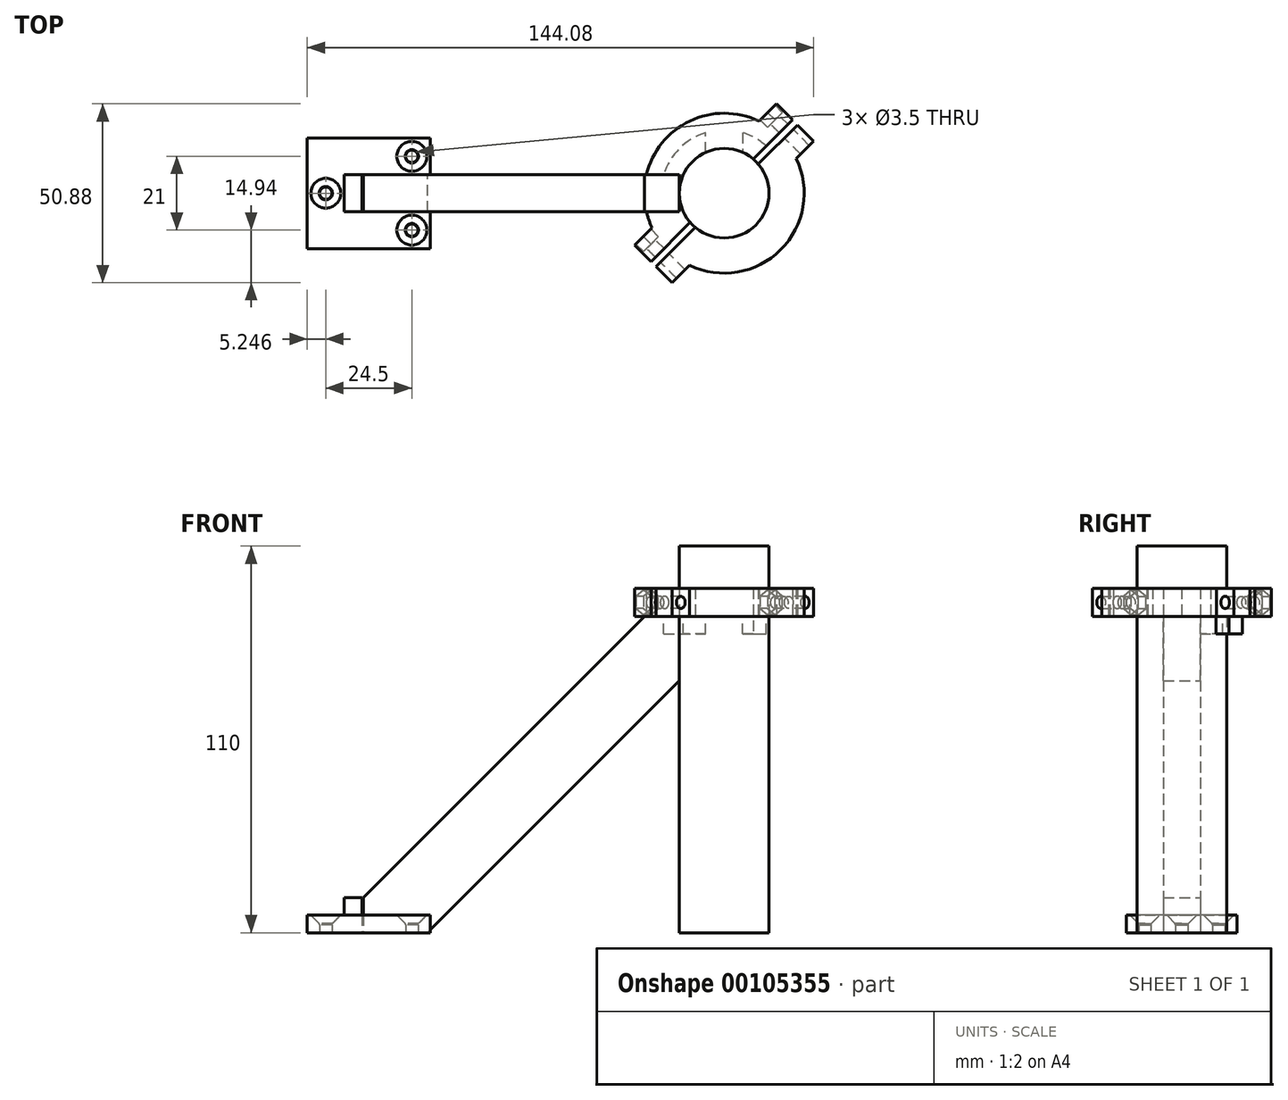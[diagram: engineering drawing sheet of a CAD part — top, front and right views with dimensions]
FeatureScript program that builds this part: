
annotation { "Feature Type Name" : "Feature", "Feature Type Description" : "" }
export const myFeature = defineFeature(function(context is Context, id is Id, definition is map)
    precondition{}
    {
        {
            var Q0;
            Q0=qCreatedBy(makeId("Top.planeOp"),FACE);
            var sketch = newSketch(context, id + "F0", { "sketchPlane" : qUnion([Q0])});
            skCircle(sketch, "E0", {"center": v(0, 0) * mm, "radius": 12.75 * mm});
            skLineSegment(sketch, "E1.bottom", {"start": v(-83.64, 15.75) * mm, "end": v(-118.64, 15.75) * mm});
            skLineSegment(sketch, "E1.top", {"start": v(-83.64, -15.75) * mm, "end": v(-118.64, -15.75) * mm});
            skLineSegment(sketch, "E1.left", {"start": v(-83.64, 15.75) * mm, "end": v(-83.64, 5.25) * mm});
            skLineSegment(sketch, "E1.right", {"start": v(-118.64, 15.75) * mm, "end": v(-118.64, -15.75) * mm});
            skLineSegment(sketch, "E2.bottom", {"start": v(-83.64, -5.25) * mm, "end": v(-108.14, -5.25) * mm});
            skLineSegment(sketch, "E2.top", {"start": v(-83.64, 5.25) * mm, "end": v(-108.14, 5.25) * mm});
            skLineSegment(sketch, "E2.right", {"start": v(-108.14, -5.25) * mm, "end": v(-108.14, 5.25) * mm});
            skCircle(sketch, "E3", {"center": v(-88.9, 10.5) * mm, "radius": 1.75 * mm});
            skCircle(sketch, "E4", {"center": v(-113.4, 0) * mm, "radius": 1.75 * mm});
            skCircle(sketch, "E5.MirrorC", {"center": v(-88.9, -10.5) * mm, "radius": 1.75 * mm});
            skCircle(sketch, "E6", {"center": v(-88.9, 10.5) * mm, "radius": 4.25 * mm, "construction": true});
            skCircle(sketch, "E7", {"center": v(-113.4, 0) * mm, "radius": 4.25 * mm, "construction": true});
            skLineSegment(sketch, "E8", {"start": v(-103.14, 5.25) * mm, "end": v(-103.14, -5.25) * mm});
            skLineSegment(sketch, "E9.trimOffspring", {"start": v(-83.64, -5.25) * mm, "end": v(-83.64, -15.75) * mm});
            skSolve(sketch);
        }
        {
            var Q0;
            Q0=makeQuery(id+"F0.imprint","IMPRINT",FACE,{"disambiguationData":[TD([[makeQuery(id+"F0.imprint","IMPRINT",EDGE,{"derivedFrom":sQuery(id+"F0.wireOp",EDGE,"E1.bottom")}),1.0]])]});
            extrude(context, id + "F1", {"entities" : qUnion([Q0]), "depth" : 5 * mm});
        }
        {
            var Q0;
            {var subQ0=sQuery(id+"F0.wireOp",EDGE,"E2.right");Q0=makeQuery(id+"F0.imprint","IMPRINT",FACE,{"disambiguationData":[TD([[makeQuery(id+"F0.imprint","IMPRINT",EDGE,{"derivedFrom":subQ0}),-1.0]])]});}
            extrude(context, id + "F2", {"entities" : qUnion([Q0]), "operationType" : NewBodyOperationType.ADD, "depth" : 10 * mm});
        }
        {
            var Q0;
            Q0=makeQuery(id+"F1.opExtrude","CAP_EDGE",EDGE,{"disambiguationData":[OSD([sQuery(id+"F0.wireOp",EDGE,"E4")])],"isStart":false});
            var Q1;
            Q1=makeQuery(id+"F1.opExtrude","CAP_EDGE",EDGE,{"disambiguationData":[OSD([sQuery(id+"F0.wireOp",EDGE,"E3")])],"isStart":false});
            var Q2;
            Q2=makeQuery(id+"F1.opExtrude","CAP_EDGE",EDGE,{"disambiguationData":[OSD([sQuery(id+"F0.wireOp",EDGE,"E5.MirrorC")])],"isStart":false});
            chamfer(context, id + "F3", {"entities" : qUnion([Q0, Q1, Q2]), "width" : 2.5 * mm, "tangentPropagation" : true});
        }
        {
            var Q0;
            {var subQ0=sQuery(id+"F0.wireOp",EDGE,"E4");Q0=makeQuery(id+"F3.opChamfer","BLEND_EDGE",EDGE,{"blendedFrom":[makeQuery(id+"F1.opExtrude","CAP_EDGE",EDGE,{"disambiguationData":[OSD([subQ0])],"isStart":false}),makeQuery(id+"F1.opExtrude","SWEPT_FACE",FACE,{"disambiguationData":[OSD([subQ0])]})],"blendedInto":[makeQuery(id+"F1.opExtrude","SWEPT_FACE",FACE,{"disambiguationData":[OSD([subQ0])]})]});}
            var Q1;
            {var subQ0=sQuery(id+"F0.wireOp",EDGE,"E3");Q1=makeQuery(id+"F3.opChamfer","BLEND_EDGE",EDGE,{"blendedFrom":[makeQuery(id+"F1.opExtrude","CAP_EDGE",EDGE,{"disambiguationData":[OSD([subQ0])],"isStart":false}),makeQuery(id+"F1.opExtrude","SWEPT_FACE",FACE,{"disambiguationData":[OSD([subQ0])]})],"blendedInto":[makeQuery(id+"F1.opExtrude","SWEPT_FACE",FACE,{"disambiguationData":[OSD([subQ0])]})]});}
            var Q2;
            {var subQ0=sQuery(id+"F0.wireOp",EDGE,"E5.MirrorC");Q2=makeQuery(id+"F3.opChamfer","BLEND_EDGE",EDGE,{"blendedFrom":[makeQuery(id+"F1.opExtrude","CAP_EDGE",EDGE,{"disambiguationData":[OSD([subQ0])],"isStart":false}),makeQuery(id+"F1.opExtrude","SWEPT_FACE",FACE,{"disambiguationData":[OSD([subQ0])]})],"blendedInto":[makeQuery(id+"F1.opExtrude","SWEPT_FACE",FACE,{"disambiguationData":[OSD([subQ0])]})]});}
            chamfer(context, id + "F4", {"entities" : qUnion([Q0, Q1, Q2]), "width" : 0.5 * mm, "tangentPropagation" : true});
        }
        {
            var Q0;
            Q0=makeQuery(id+"F0.imprint","IMPRINT",FACE,{"disambiguationData":[TD([[makeQuery(id+"F0.imprint","IMPRINT",EDGE,{"derivedFrom":sQuery(id+"F0.wireOp",EDGE,"E0")}),1.0]])]});
            extrude(context, id + "F5", {"entities" : qUnion([Q0]), "depth" : 110 * mm});
        }
        {
            var Q0;
            Q0=qCreatedBy(makeId("Front.planeOp"),FACE);
            var sketch = newSketch(context, id + "F6", { "sketchPlane" : qUnion([Q0])});
            skLineSegment(sketch, "E10", {"start": v(-12.75, 0) * mm, "end": v(-12.75, 90) * mm});
            skLineSegment(sketch, "E11", {"start": v(-12.75, 71.72) * mm, "end": v(-84.47, 0) * mm});
            skLineSegment(sketch, "E12", {"start": v(-22.75, 90) * mm, "end": v(-102.75, 10) * mm});
            skLineSegment(sketch, "E13", {"start": v(-102.75, 10) * mm, "end": v(-102.75, 0) * mm});
            skLineSegment(sketch, "E14", {"start": v(-102.75, 0) * mm, "end": v(-84.47, 0) * mm});
            skLineSegment(sketch, "E15", {"start": v(-22.75, 90) * mm, "end": v(-12.75, 90) * mm});
            skSolve(sketch);
        }
        {
            var Q0;
            Q0 = qSketchRegion(id + "F6", true);
            extrude(context, id + "F7", {"entities" : qUnion([Q0]), "endBound" : BoundingType.SYMMETRIC, "depth" : 10.5 * mm});
        }
        {
            var Q0;
            Q0=makeQuery(id+"F7.opExtrude","SWEPT_FACE",FACE,{"disambiguationData":[OSD([sQuery(id+"F6.wireOp",EDGE,"E15")])]});
            var sketch = newSketch(context, id + "F8", { "sketchPlane" : qUnion([Q0])});
            skCircle(sketch, "E16.0", {"center": v(0, 0) * mm, "radius": 12.75 * mm});
            skLineSegment(sketch, "E17.0", {"start": v(-22.75, -5.25) * mm, "end": v(-22.75, 5.25) * mm, "construction": true});
            skPoint(sketch, "E18", {"position": v(-22.75, 0) * mm});
            skLineSegment(sketch, "E19", {"start": v(-33.02, -33.02) * mm, "end": v(44.09, 44.09) * mm, "construction": true});
            skLineSegment(sketch, "E20", {"start": v(8.28, 9.7) * mm, "end": v(19.43, 20.84) * mm});
            skLineSegment(sketch, "E21", {"start": v(19.43, 20.84) * mm, "end": v(14.83, 25.44) * mm});
            skLineSegment(sketch, "E22", {"start": v(14.83, 25.44) * mm, "end": v(9.88, 20.5) * mm});
            skLineSegment(sketch, "E23", {"start": v(30.41, -30.41) * mm, "end": v(-33.98, 33.98) * mm, "construction": true});
            skLineSegment(sketch, "E24.MirrorCS", {"start": v(-25.44, -14.83) * mm, "end": v(-20.5, -9.88) * mm});
            skLineSegment(sketch, "E25.MirrorCS", {"start": v(-20.84, -19.43) * mm, "end": v(-25.44, -14.83) * mm});
            skLineSegment(sketch, "E26.MirrorCS", {"start": v(-9.7, -8.28) * mm, "end": v(-20.84, -19.43) * mm});
            skArc(sketch, "E27", {"start": v(-20.5, -9.88) * mm, "mid": v(-22.43, 3.8) * mm, "end": v(-16.09, 16.09) * mm});
            skArc(sketch, "E28.MirrorCS", {"start": v(9.88, 20.5) * mm, "mid": v(-3.8, 22.43) * mm, "end": v(-16.09, 16.09) * mm});
            skLineSegment(sketch, "E29.MirrorCS", {"start": v(9.7, 8.28) * mm, "end": v(20.84, 19.43) * mm});
            skLineSegment(sketch, "E30.MirrorCS", {"start": v(20.84, 19.43) * mm, "end": v(25.44, 14.83) * mm});
            skLineSegment(sketch, "E31.MirrorCS", {"start": v(25.44, 14.83) * mm, "end": v(20.5, 9.88) * mm});
            skArc(sketch, "E32.MirrorCS", {"start": v(20.5, 9.88) * mm, "mid": v(22.43, -3.8) * mm, "end": v(16.09, -16.09) * mm});
            skArc(sketch, "E33.MirrorCS", {"start": v(-9.88, -20.5) * mm, "mid": v(3.8, -22.43) * mm, "end": v(16.09, -16.09) * mm});
            skLineSegment(sketch, "E34.MirrorCS", {"start": v(-14.83, -25.44) * mm, "end": v(-9.88, -20.5) * mm});
            skLineSegment(sketch, "E35.MirrorCS", {"start": v(-19.43, -20.84) * mm, "end": v(-14.83, -25.44) * mm});
            skLineSegment(sketch, "E36.MirrorCS", {"start": v(-8.28, -9.7) * mm, "end": v(-19.43, -20.84) * mm});
            skSolve(sketch);
        }
        {
            var Q0;
            {var subQ0=sQuery(id+"F8.wireOp",EDGE,"E20");Q0=makeQuery(id+"F8.imprint","IMPRINT",FACE,{"disambiguationData":[TD([[makeQuery(id+"F8.imprint","IMPRINT",EDGE,{"derivedFrom":subQ0}),1.0]])]});}
            var Q1;
            {var subQ0=sQuery(id+"F8.wireOp",EDGE,"E29.MirrorCS");Q1=makeQuery(id+"F8.imprint","IMPRINT",FACE,{"disambiguationData":[TD([[makeQuery(id+"F8.imprint","IMPRINT",EDGE,{"derivedFrom":subQ0}),-1.0]])]});}
            var Q2;
            {var subQ0=sQuery(id+"F6.wireOp",EDGE,"E15");var subQ1=makeQuery(id+"F7.opExtrude","CAP_EDGE",EDGE,{"disambiguationData":[OSD([subQ0])],"isStart":false});var subQ5=sQuery(id+"F8.wireOp",EDGE,"E27");var subQ10=makeQuery(id+"F8.imprint","INTERSECT",VERTEX,{"derivedFrom":[subQ1,subQ5]});Q2=makeQuery(id+"F8.imprint","IMPRINT",FACE,{"disambiguationData":[TD([[makeQuery(id+"F8.imprint","IMPRINT",EDGE,{"disambiguationData":[TD([[subQ10,-1.0]])],"derivedFrom":subQ5}),-1.0]])]});}
            var Q3;
            {var subQ7=sQuery(id+"F8.wireOp",EDGE,"E24.MirrorCS");Q3=makeQuery(id+"F8.imprint","IMPRINT",FACE,{"disambiguationData":[TD([[makeQuery(id+"F8.imprint","IMPRINT",EDGE,{"derivedFrom":subQ7}),-1.0]])]});}
            extrude(context, id + "F9", {"entities" : qUnion([Q0, Q1, Q2, Q3]), "depth" : 8 * mm});
        }
        {
            var Q0;
            Q0=makeQuery(id+"F9.opExtrude","CAP_FACE",FACE,{"disambiguationData":[OSD([sQuery(id+"F8.wireOp",EDGE,"E16.0"),sQuery(id+"F8.wireOp",EDGE,"E20"),sQuery(id+"F8.wireOp",EDGE,"E21"),sQuery(id+"F8.wireOp",EDGE,"E22"),sQuery(id+"F8.wireOp",EDGE,"E24.MirrorCS"),sQuery(id+"F8.wireOp",EDGE,"E25.MirrorCS"),sQuery(id+"F8.wireOp",EDGE,"E26.MirrorCS"),sQuery(id+"F8.wireOp",EDGE,"E27"),sQuery(id+"F8.wireOp",EDGE,"E28.MirrorCS")])],"isStart":true});
            var sketch = newSketch(context, id + "F10", { "sketchPlane" : qUnion([Q0])});
            skLineSegment(sketch, "E37.0", {"start": v(30.41, 30.41) * mm, "end": v(-33.98, -33.98) * mm, "construction": true});
            skLineSegment(sketch, "E38.0", {"start": v(-12.75, -5.25) * mm, "end": v(-84.47, -5.25) * mm});
            skLineSegment(sketch, "E39.0", {"start": v(-12.75, 5.25) * mm, "end": v(-84.47, 5.25) * mm});
            skLineSegment(sketch, "E40.0", {"start": v(-9.7, 8.28) * mm, "end": v(-20.84, 19.43) * mm});
            skLineSegment(sketch, "E41", {"start": v(-12.75, 5.25) * mm, "end": v(-11.62, 5.25) * mm});
            skLineSegment(sketch, "E42", {"start": v(-12.75, -5.25) * mm, "end": v(-11.62, -5.25) * mm});
            skArc(sketch, "E43", {"start": v(-13.42, 12) * mm, "mid": v(-15.68, 8.83) * mm, "end": v(-17.22, 5.25) * mm});
            skArc(sketch, "E44", {"start": v(-17.22, -5.25) * mm, "mid": v(-15.43, -9.26) * mm, "end": v(-12.73, -12.73) * mm});
            skArc(sketch, "E45.MirrorCS", {"start": v(-5.25, -17.22) * mm, "mid": v(-9.26, -15.43) * mm, "end": v(-12.73, -12.73) * mm});
            skLineSegment(sketch, "E46.MirrorCS", {"start": v(-5.25, -12.75) * mm, "end": v(-5.25, -84.47) * mm});
            skLineSegment(sketch, "E47.MirrorCS", {"start": v(-5.25, -12.75) * mm, "end": v(-5.25, -11.62) * mm});
            skLineSegment(sketch, "E48.MirrorCS", {"start": v(5.25, -12.75) * mm, "end": v(5.25, -11.62) * mm});
            skLineSegment(sketch, "E49.MirrorCS", {"start": v(5.25, -12.75) * mm, "end": v(5.25, -84.47) * mm});
            skArc(sketch, "E50.MirrorCS", {"start": v(12, -13.42) * mm, "mid": v(8.83, -15.68) * mm, "end": v(5.25, -17.22) * mm});
            skLineSegment(sketch, "E51.MirrorCS", {"start": v(8.28, -9.7) * mm, "end": v(19.43, -20.84) * mm});
            skSolve(sketch);
        }
        {
            var Q0;
            {var subQ6=sQuery(id+"F10.wireOp",EDGE,"E41");Q0=makeQuery(id+"F10.imprint","IMPRINT",FACE,{"disambiguationData":[TD([[makeQuery(id+"F10.imprint","IMPRINT",EDGE,{"derivedFrom":subQ6}),1.0]])]});}
            var Q1;
            {var subQ1=sQuery(id+"F10.wireOp",EDGE,"E42");Q1=makeQuery(id+"F10.imprint","IMPRINT",FACE,{"disambiguationData":[TD([[makeQuery(id+"F10.imprint","IMPRINT",EDGE,{"derivedFrom":subQ1}),-1.0]])]});}
            var Q2;
            {var subQ6=sQuery(id+"F10.wireOp",EDGE,"E48.MirrorCS");Q2=makeQuery(id+"F10.imprint","IMPRINT",FACE,{"disambiguationData":[TD([[makeQuery(id+"F10.imprint","IMPRINT",EDGE,{"derivedFrom":subQ6}),-1.0]])]});}
            extrude(context, id + "F11", {"entities" : qUnion([Q0, Q1, Q2]), "operationType" : NewBodyOperationType.ADD, "depth" : 5 * mm});
        }
        {
            var Q0;
            Q0=makeQuery(id+"F9.opExtrude","SWEPT_FACE",FACE,{"disambiguationData":[OSD([sQuery(id+"F8.wireOp",EDGE,"E22")])]});
            var sketch = newSketch(context, id + "F12", { "sketchPlane" : qUnion([Q0])});
            skPoint(sketch, "E52.0", {"position": v(-28.48, 98) * mm});
            skPoint(sketch, "E53.0", {"position": v(-21.48, 90) * mm});
            skPoint(sketch, "E54.0", {"position": v(21.48, 98) * mm});
            skPoint(sketch, "E55.0", {"position": v(28.48, 90) * mm});
            skLineSegment(sketch, "E56", {"start": v(-28.48, 98) * mm, "end": v(-21.48, 90) * mm, "construction": true});
            skLineSegment(sketch, "E57", {"start": v(21.48, 98) * mm, "end": v(28.48, 90) * mm, "construction": true});
            skCircle(sketch, "E58", {"center": v(-24.98, 94) * mm, "radius": 1.75 * mm});
            skCircle(sketch, "E59", {"center": v(24.98, 94) * mm, "radius": 1.75 * mm});
            skCircle(sketch, "E60.cCircle", {"center": v(-24.98, 94) * mm, "radius": 3 * mm, "construction": true});
            skLineSegment(sketch, "E60.0", {"start": v(-27.98, 92.27) * mm, "end": v(-27.98, 95.73) * mm});
            skLineSegment(sketch, "E60.1", {"start": v(-27.98, 95.73) * mm, "end": v(-24.98, 97.46) * mm});
            skLineSegment(sketch, "E60.2", {"start": v(-24.98, 97.46) * mm, "end": v(-21.98, 95.73) * mm});
            skLineSegment(sketch, "E60.3", {"start": v(-21.98, 95.73) * mm, "end": v(-21.98, 92.27) * mm});
            skLineSegment(sketch, "E60.4", {"start": v(-21.98, 92.27) * mm, "end": v(-24.98, 90.54) * mm});
            skLineSegment(sketch, "E60.5", {"start": v(-24.98, 90.54) * mm, "end": v(-27.98, 92.27) * mm});
            skPoint(sketch, "E60.0.midPoint", {"position": v(-27.98, 94) * mm});
            skCircle(sketch, "E61.cCircle", {"center": v(24.98, 94) * mm, "radius": 3 * mm, "construction": true});
            skPoint(sketch, "E61.cCircle.perimeterSnap0", {"position": v(-28.48, 94) * mm});
            skLineSegment(sketch, "E61.0", {"start": v(21.98, 92.27) * mm, "end": v(21.98, 95.73) * mm});
            skLineSegment(sketch, "E61.1", {"start": v(21.98, 95.73) * mm, "end": v(24.98, 97.46) * mm});
            skLineSegment(sketch, "E61.2", {"start": v(24.98, 97.46) * mm, "end": v(27.98, 95.73) * mm});
            skLineSegment(sketch, "E61.3", {"start": v(27.98, 95.73) * mm, "end": v(27.98, 92.27) * mm});
            skLineSegment(sketch, "E61.4", {"start": v(27.98, 92.27) * mm, "end": v(24.98, 90.54) * mm});
            skLineSegment(sketch, "E61.5", {"start": v(24.98, 90.54) * mm, "end": v(21.98, 92.27) * mm});
            skPoint(sketch, "E61.0.midPoint", {"position": v(21.98, 94) * mm});
            skPoint(sketch, "E61.0.midPoint.positionSnap0", {"position": v(-28.48, 94) * mm});
            skSolve(sketch);
        }
        {
            var Q0;
            Q0 = qSketchRegion(id + "F12", true);
            extrude(context, id + "F13", {"entities" : qUnion([Q0]), "operationType" : NewBodyOperationType.REMOVE, "oppositeDirection" : true, "depth" : 3 * mm});
        }
        {
            var Q0;
            Q0=makeQuery(id+"F12.imprint","IMPRINT",FACE,{"disambiguationData":[TD([[makeQuery(id+"F12.imprint","IMPRINT",EDGE,{"derivedFrom":sQuery(id+"F12.wireOp",EDGE,"E58")}),1.0]])]});
            var Q1;
            Q1=makeQuery(id+"F12.imprint","IMPRINT",FACE,{"disambiguationData":[TD([[makeQuery(id+"F12.imprint","IMPRINT",EDGE,{"derivedFrom":sQuery(id+"F12.wireOp",EDGE,"E59")}),1.0]])]});
            extrude(context, id + "F14", {"entities" : qUnion([Q0, Q1]), "operationType" : NewBodyOperationType.REMOVE, "endBound" : BoundingType.THROUGH_ALL, "oppositeDirection" : true, "depth" : 25 * mm});
        }
    });
